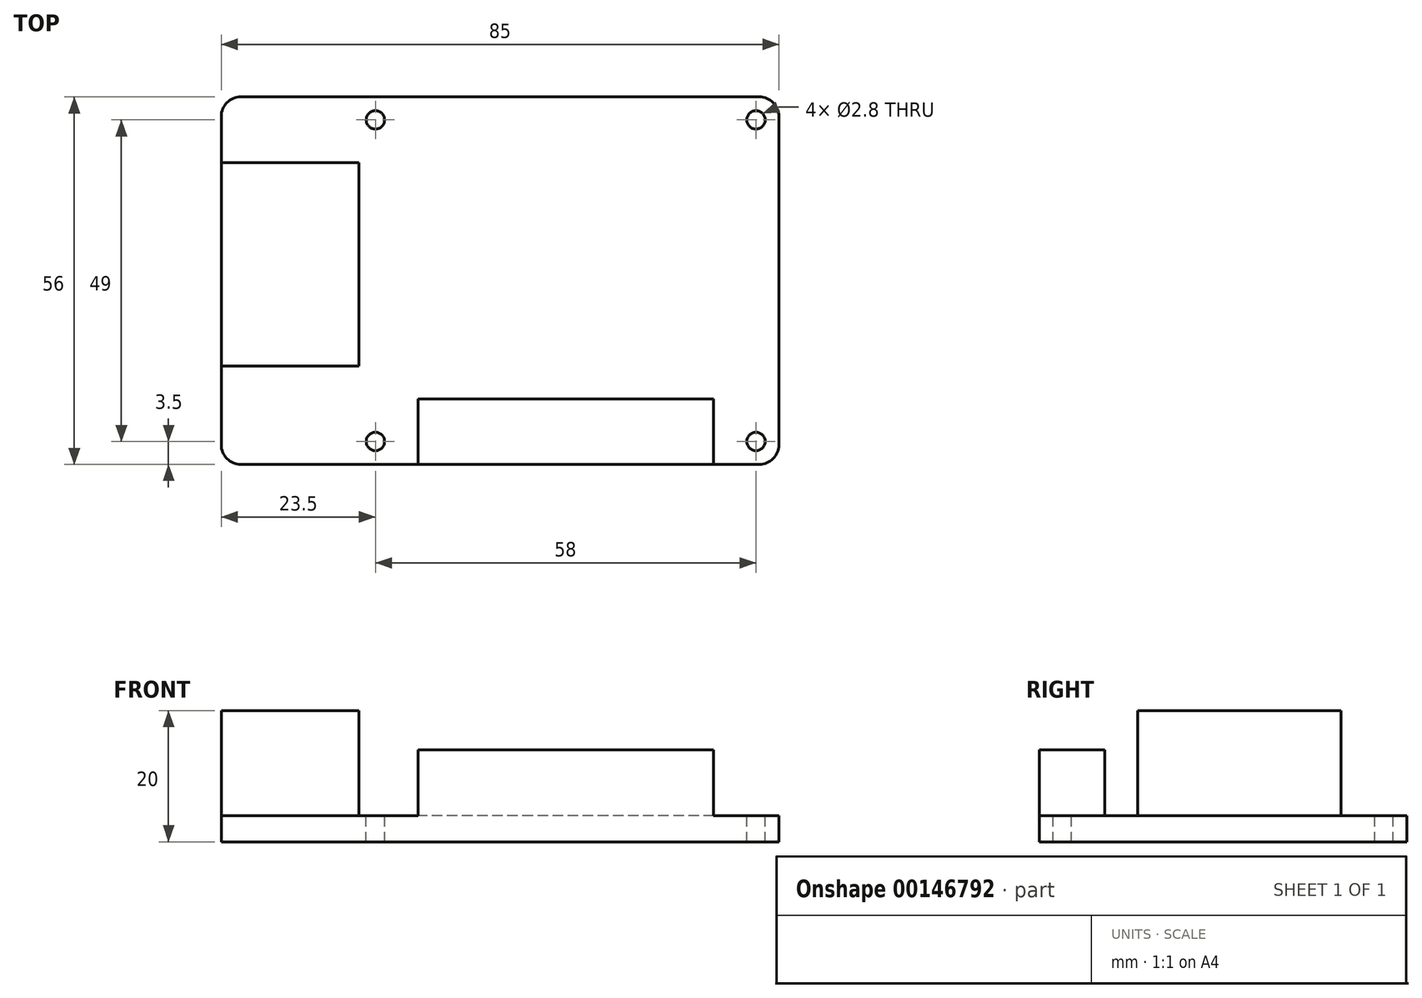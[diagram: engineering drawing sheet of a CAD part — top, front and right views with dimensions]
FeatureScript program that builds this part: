
annotation { "Feature Type Name" : "Feature", "Feature Type Description" : "" }
export const myFeature = defineFeature(function(context is Context, id is Id, definition is map)
    precondition{}
    {
        {
            var Q0;
            Q0=qCreatedBy(makeId("Top.planeOp"),FACE);
            var sketch = newSketch(context, id + "F0", { "sketchPlane" : qUnion([Q0])});
            skLineSegment(sketch, "E0.bottom", {"start": v(39.5, -28) * mm, "end": v(-39.5, -28) * mm});
            skLineSegment(sketch, "E0.top", {"start": v(39.5, 28) * mm, "end": v(-39.5, 28) * mm});
            skLineSegment(sketch, "E0.left", {"start": v(42.5, -25) * mm, "end": v(42.5, 25) * mm});
            skLineSegment(sketch, "E0.right", {"start": v(-42.5, -25) * mm, "end": v(-42.5, 25) * mm});
            skPoint(sketch, "E0.middle", {"position": v(0, 0) * mm});
            skPoint(sketch, "E1.visualSharp", {"position": v(-42.5, 28) * mm});
            skArc(sketch, "E1.filletArc", {"start": v(-39.5, 28) * mm, "mid": v(-41.62, 27.12) * mm, "end": v(-42.5, 25) * mm});
            skPoint(sketch, "E2.visualSharp", {"position": v(-42.5, -28) * mm});
            skArc(sketch, "E2.filletArc", {"start": v(-42.5, -25) * mm, "mid": v(-41.62, -27.12) * mm, "end": v(-39.5, -28) * mm});
            skPoint(sketch, "E3.visualSharp", {"position": v(42.5, -28) * mm});
            skArc(sketch, "E3.filletArc", {"start": v(39.5, -28) * mm, "mid": v(41.62, -27.12) * mm, "end": v(42.5, -25) * mm});
            skPoint(sketch, "E4.visualSharp", {"position": v(42.5, 28) * mm});
            skArc(sketch, "E4.filletArc", {"start": v(42.5, 25) * mm, "mid": v(41.62, 27.12) * mm, "end": v(39.5, 28) * mm});
            skSolve(sketch);
        }
        {
            var Q0;
            Q0 = qSketchRegion(id + "F0", true);
            extrude(context, id + "F1", {"entities" : qUnion([Q0]), "depth" : 20 * mm});
        }
        {
            var Q0;
            Q0=makeQuery(id+"F1.opExtrude","CAP_FACE",FACE,{"disambiguationData":[OSD([sQuery(id+"F0.wireOp",EDGE,"E0.bottom"),sQuery(id+"F0.wireOp",EDGE,"E0.top"),sQuery(id+"F0.wireOp",EDGE,"E0.left"),sQuery(id+"F0.wireOp",EDGE,"E0.right"),sQuery(id+"F0.wireOp",EDGE,"E1.filletArc"),sQuery(id+"F0.wireOp",EDGE,"E2.filletArc"),sQuery(id+"F0.wireOp",EDGE,"E3.filletArc"),sQuery(id+"F0.wireOp",EDGE,"E4.filletArc")])],"isStart":false});
            var sketch = newSketch(context, id + "F2", { "sketchPlane" : qUnion([Q0])});
            skCircle(sketch, "E5", {"center": v(-19, 24.5) * mm, "radius": 1.4 * mm});
            skCircle(sketch, "E6.MirrorC", {"center": v(39, 24.5) * mm, "radius": 1.4 * mm});
            skCircle(sketch, "E7.MirrorC", {"center": v(-19, -24.5) * mm, "radius": 1.4 * mm});
            skCircle(sketch, "E8.MirrorC", {"center": v(39, -24.5) * mm, "radius": 1.4 * mm});
            skSolve(sketch);
        }
        {
            var Q0;
            Q0 = qSketchRegion(id + "F2", true);
            extrude(context, id + "F3", {"entities" : qUnion([Q0]), "operationType" : NewBodyOperationType.REMOVE, "oppositeDirection" : true, "depth" : 25 * mm});
        }
        {
            var Q0;
            Q0=makeQuery(id+"F1.opExtrude","CAP_FACE",FACE,{"disambiguationData":[OSD([sQuery(id+"F0.wireOp",EDGE,"E0.bottom"),sQuery(id+"F0.wireOp",EDGE,"E0.top"),sQuery(id+"F0.wireOp",EDGE,"E0.left"),sQuery(id+"F0.wireOp",EDGE,"E0.right"),sQuery(id+"F0.wireOp",EDGE,"E1.filletArc"),sQuery(id+"F0.wireOp",EDGE,"E2.filletArc"),sQuery(id+"F0.wireOp",EDGE,"E3.filletArc"),sQuery(id+"F0.wireOp",EDGE,"E4.filletArc")])],"isStart":false});
            var sketch = newSketch(context, id + "F4", { "sketchPlane" : qUnion([Q0])});
            skLineSegment(sketch, "E9.bottom", {"start": v(42.5, 28) * mm, "end": v(-21.5, 28) * mm});
            skLineSegment(sketch, "E9.top", {"start": v(42.5, -28) * mm, "end": v(-21.5, -28) * mm});
            skLineSegment(sketch, "E9.left", {"start": v(42.5, 28) * mm, "end": v(42.5, -28) * mm});
            skLineSegment(sketch, "E9.right", {"start": v(-21.5, 28) * mm, "end": v(-21.5, -28) * mm});
            skLineSegment(sketch, "E10.bottom", {"start": v(-21.5, 28) * mm, "end": v(-42.5, 28) * mm});
            skLineSegment(sketch, "E10.top", {"start": v(-21.5, 18) * mm, "end": v(-42.5, 18) * mm});
            skLineSegment(sketch, "E10.right", {"start": v(-42.5, 28) * mm, "end": v(-42.5, 18) * mm});
            skLineSegment(sketch, "E11.bottom", {"start": v(-21.5, -28) * mm, "end": v(-42.5, -28) * mm});
            skLineSegment(sketch, "E11.top", {"start": v(-21.5, -13) * mm, "end": v(-42.5, -13) * mm});
            skLineSegment(sketch, "E11.right", {"start": v(-42.5, -28) * mm, "end": v(-42.5, -13) * mm});
            skSolve(sketch);
        }
        {
            var Q0;
            Q0 = qSketchRegion(id + "F4", true);
            extrude(context, id + "F5", {"entities" : qUnion([Q0]), "operationType" : NewBodyOperationType.REMOVE, "oppositeDirection" : true, "depth" : 16 * mm});
        }
        {
            var Q0;
            Q0=makeQuery(id+"F5.boolean.opBoolean","COPY",FACE,{"derivedFrom":makeQuery(id+"F5.opExtrude","CAP_FACE",FACE,{"disambiguationData":[OSD([sQuery(id+"F4.wireOp",EDGE,"E9.bottom"),sQuery(id+"F4.wireOp",EDGE,"E9.top"),sQuery(id+"F4.wireOp",EDGE,"E9.left"),sQuery(id+"F4.wireOp",EDGE,"E9.right"),sQuery(id+"F4.wireOp",EDGE,"E10.bottom"),sQuery(id+"F4.wireOp",EDGE,"E10.top"),sQuery(id+"F4.wireOp",EDGE,"E10.right"),sQuery(id+"F4.wireOp",EDGE,"E11.bottom"),sQuery(id+"F4.wireOp",EDGE,"E11.top"),sQuery(id+"F4.wireOp",EDGE,"E11.right")])],"isStart":false})});
            var sketch = newSketch(context, id + "F6", { "sketchPlane" : qUnion([Q0])});
            skLineSegment(sketch, "E12.bottom", {"start": v(32.5, -28) * mm, "end": v(-12.5, -28) * mm});
            skLineSegment(sketch, "E12.top", {"start": v(32.5, -18) * mm, "end": v(-12.5, -18) * mm});
            skLineSegment(sketch, "E12.left", {"start": v(32.5, -28) * mm, "end": v(32.5, -18) * mm});
            skLineSegment(sketch, "E12.right", {"start": v(-12.5, -28) * mm, "end": v(-12.5, -18) * mm});
            skSolve(sketch);
        }
        {
            var Q0;
            Q0 = qSketchRegion(id + "F6", true);
            extrude(context, id + "F7", {"entities" : qUnion([Q0]), "operationType" : NewBodyOperationType.ADD, "depth" : 10 * mm});
        }
    });
